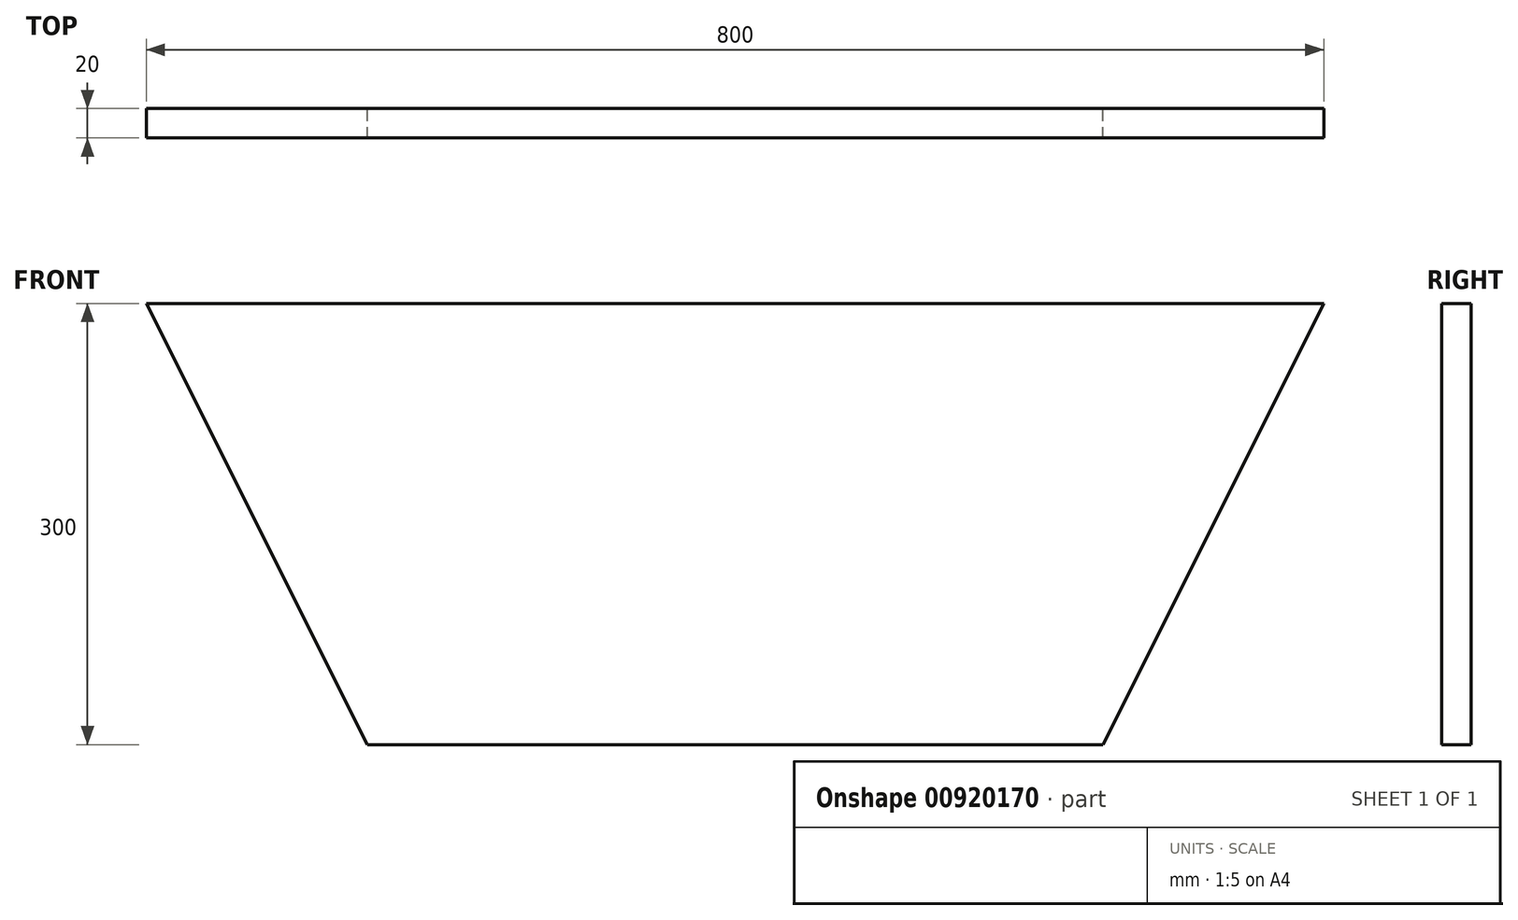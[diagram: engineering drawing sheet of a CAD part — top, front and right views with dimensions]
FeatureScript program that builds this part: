
annotation { "Feature Type Name" : "Feature", "Feature Type Description" : "" }
export const myFeature = defineFeature(function(context is Context, id is Id, definition is map)
    precondition{}
    {
        {
            var Q0;
            Q0=qCreatedBy(makeId("Front.planeOp"),FACE);
            var sketch = newSketch(context, id + "F0", { "sketchPlane" : qUnion([Q0])});
            skLineSegment(sketch, "E0", {"start": v(-250, -214.06) * mm, "end": v(250, -214.06) * mm});
            skLineSegment(sketch, "E1", {"start": v(399.2, 84.34) * mm, "end": v(250, -214.06) * mm});
            skLineSegment(sketch, "E2", {"start": v(-399.2, 84.34) * mm, "end": v(-250, -214.06) * mm});
            skLineSegment(sketch, "E3", {"start": v(-400, 85.94) * mm, "end": v(-399.2, 84.34) * mm});
            skLineSegment(sketch, "E4", {"start": v(399.2, 84.34) * mm, "end": v(400, 85.94) * mm});
            skLineSegment(sketch, "E5", {"start": v(400, 85.94) * mm, "end": v(-400, 85.94) * mm});
            skSolve(sketch);
        }
        {
            var Q0;
            Q0=qSketchRegion(id+"F0",true);
            extrude(context, id + "F1", {"entities" : qUnion([Q0]), "depth" : 20 * mm, "offsetDistance" : 25 * mm});
        }
    });
